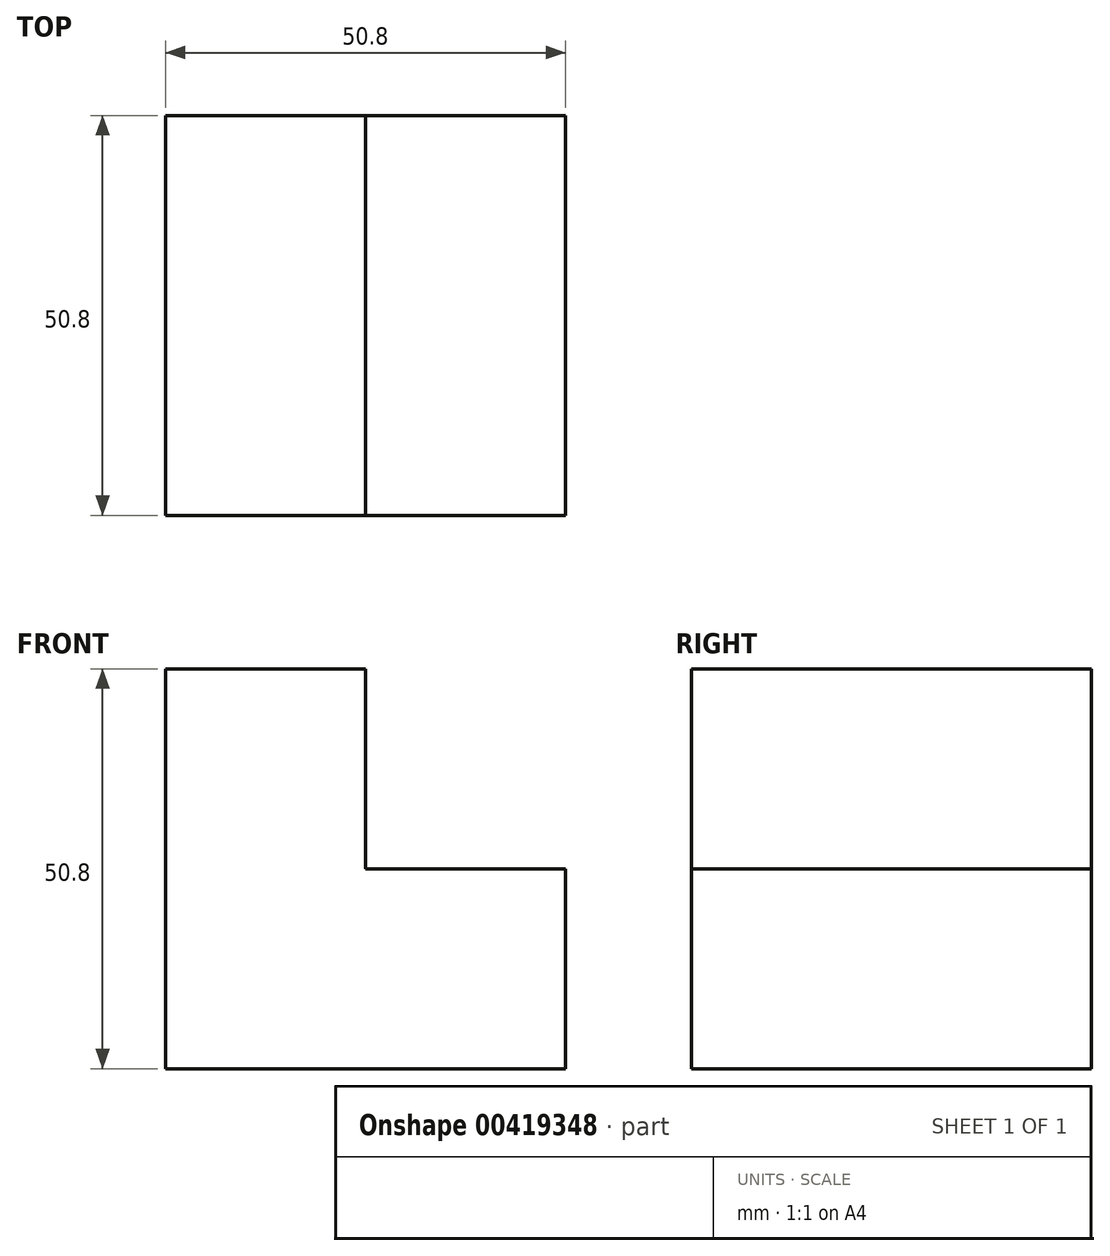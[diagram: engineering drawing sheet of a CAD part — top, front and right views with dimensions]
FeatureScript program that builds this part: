
annotation { "Feature Type Name" : "Feature", "Feature Type Description" : "" }
export const myFeature = defineFeature(function(context is Context, id is Id, definition is map)
    precondition{}
    {
        {
            var Q0;
            Q0=qCreatedBy(makeId("Front.planeOp"),FACE);
            var sketch = newSketch(context, id + "F0", { "sketchPlane" : qUnion([Q0])});
            skLineSegment(sketch, "E0", {"start": v(-53.28, 22.73) * mm, "end": v(-53.28, -28.07) * mm});
            skLineSegment(sketch, "E1", {"start": v(-53.28, -28.07) * mm, "end": v(-2.48, -28.07) * mm});
            skLineSegment(sketch, "E2", {"start": v(-2.48, -28.07) * mm, "end": v(-2.48, -2.67) * mm});
            skLineSegment(sketch, "E3", {"start": v(-2.48, -2.67) * mm, "end": v(-27.88, -2.67) * mm});
            skLineSegment(sketch, "E4", {"start": v(-27.88, -2.67) * mm, "end": v(-27.88, 22.73) * mm});
            skLineSegment(sketch, "E5", {"start": v(-27.88, 22.73) * mm, "end": v(-53.28, 22.73) * mm});
            skSolve(sketch);
        }
        {
            var Q0;
            Q0 = qSketchRegion(id + "F0", true);
            extrude(context, id + "F1", {"entities" : qUnion([Q0]), "depth" : 50.8 * mm});
        }
    });
